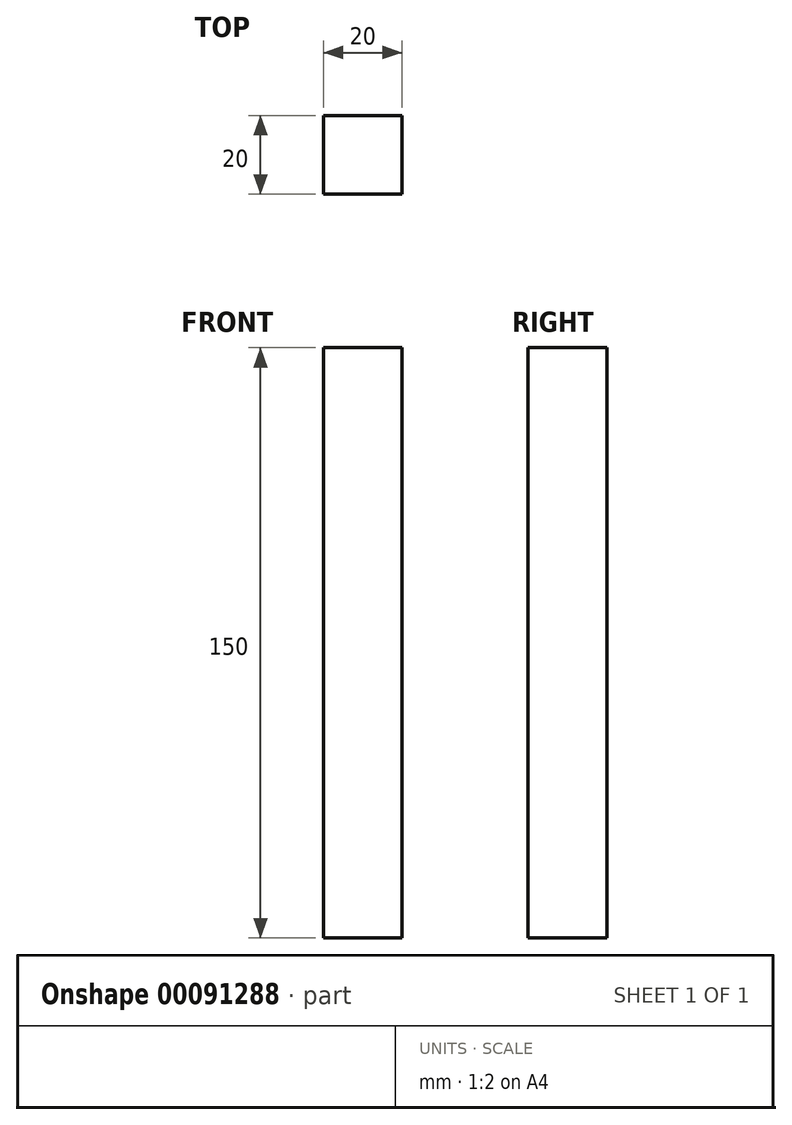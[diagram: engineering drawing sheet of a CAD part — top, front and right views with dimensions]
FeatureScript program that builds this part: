
annotation { "Feature Type Name" : "Feature", "Feature Type Description" : "" }
export const myFeature = defineFeature(function(context is Context, id is Id, definition is map)
    precondition{}
    {
        {
            var Q0;
            Q0=qCreatedBy(makeId("Top.planeOp"),FACE);
            var sketch = newSketch(context, id + "F0", { "sketchPlane" : qUnion([Q0])});
            skLineSegment(sketch, "E0.bottom", {"start": v(0, 0) * mm, "end": v(20, 0) * mm});
            skLineSegment(sketch, "E0.top", {"start": v(0, 20) * mm, "end": v(20, 20) * mm});
            skLineSegment(sketch, "E0.left", {"start": v(0, 0) * mm, "end": v(0, 20) * mm});
            skLineSegment(sketch, "E0.right", {"start": v(20, 0) * mm, "end": v(20, 20) * mm});
            skSolve(sketch);
        }
        {
            var Q0;
            Q0=makeQuery(id+"F0.imprint","IMPRINT",FACE,{"disambiguationData":[TD([[makeQuery(id+"F0.imprint","IMPRINT",EDGE,{"derivedFrom":sQuery(id+"F0.wireOp",EDGE,"E0.bottom")}),1.0]])]});
            extrude(context, id + "F1", {"entities" : qUnion([Q0]), "depth" : 150 * mm});
        }
    });
